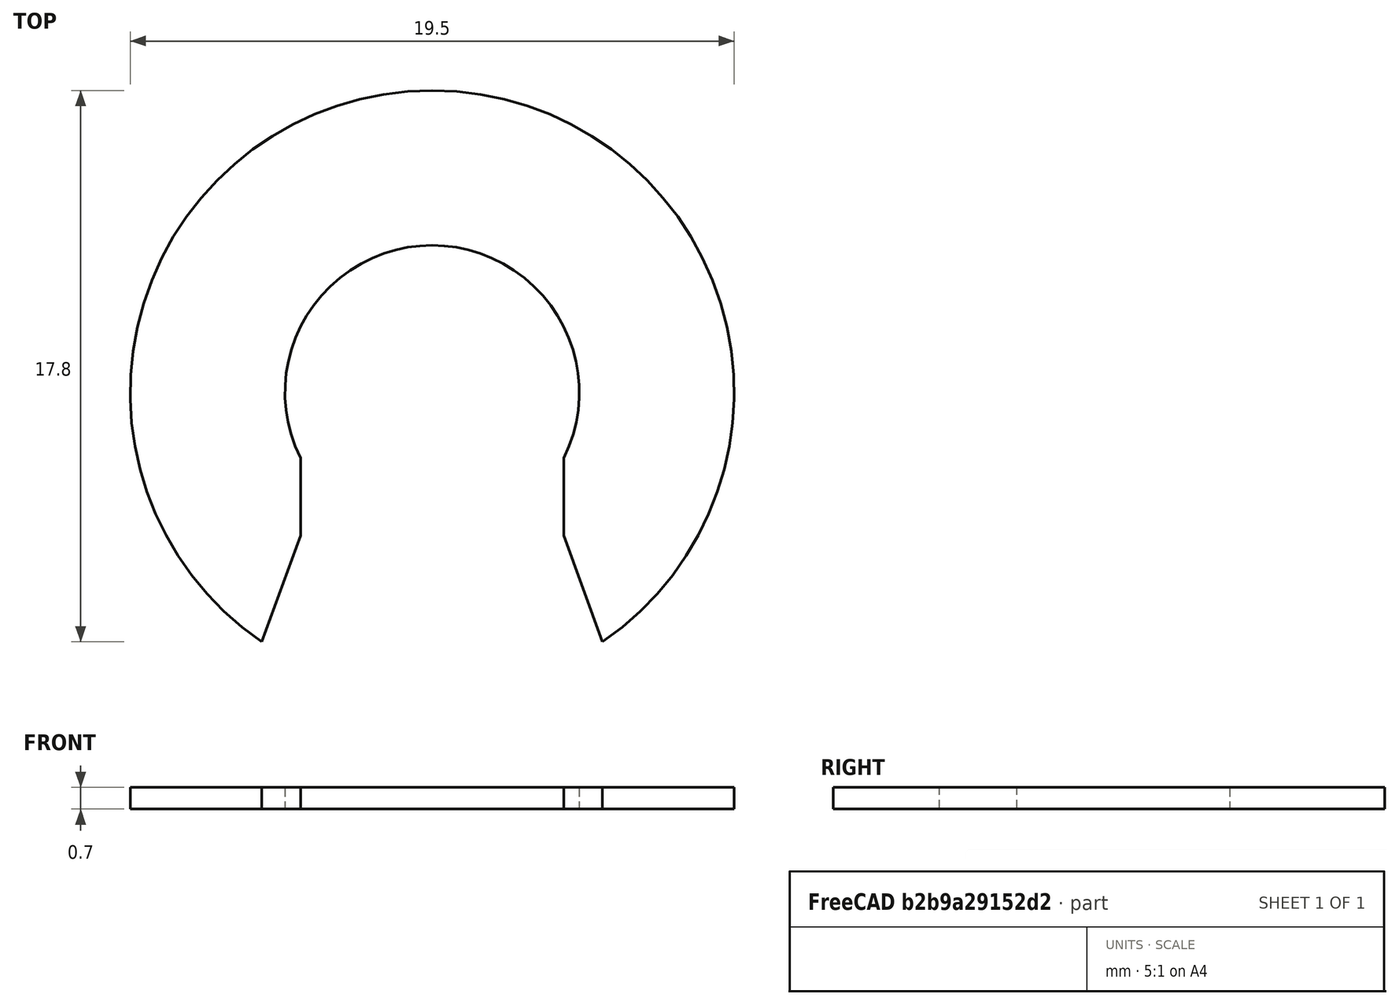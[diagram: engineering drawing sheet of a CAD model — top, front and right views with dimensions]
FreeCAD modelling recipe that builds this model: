
FCSTD DOCUMENT  (FreeCAD 0.21R30193 (Git))
Label: Clip
License: All rights reserved
LicenseURL: http://en.wikipedia.org/wiki/All_rights_reserved
objects: Sketcher::SketchObject×1, Part::Extrusion×1
note: 2 computed .brp shape members not serialized (recipe doc carries the construction recipe); baked Part::Feature solids carry a one-line shape summary decoded from their .brp

FEATURE [Sketcher::SketchObject] Sketch
  FullyConstrained = true
  sketch-geometry (6):
    g0: ArcOfCircle CenterX=0 CenterY=0 CenterZ=0 NormalX=0 NormalY=0 NormalZ=1 AngleXU=0 Radius=9.75 StartAngle=5.31173 EndAngle=10.3962
    g1: ArcOfCircle CenterX=0 CenterY=0 CenterZ=0 NormalX=0 NormalY=0 NormalZ=1 AngleXU=0 Radius=4.75 StartAngle=5.82023 EndAngle=9.88773
    g2: LineSegment StartX=-4.25 StartY=-2.12132 StartZ=0 EndX=-4.25 EndY=-4.62132 EndZ=0
    g3: LineSegment StartX=4.25 StartY=-2.12132 StartZ=0 EndX=4.25 EndY=-4.62132 EndZ=0
    g4: LineSegment StartX=4.25 StartY=-4.62132 StartZ=0 EndX=5.5 EndY=-8.05062 EndZ=0
    g5: LineSegment StartX=-5.5 StartY=-8.05062 StartZ=0 EndX=-4.25 EndY=-4.62132 EndZ=0
  constraints (17):
    c: Coincident(g0,g-1)
    c: Coincident(g1,g0)
    c: Coincident(g2,g1)
    c: Vertical(g2)
    c: Coincident(g3,g1)
    c: Vertical(g3)
    c: Coincident(g4,g3)
    c: Coincident(g4,g0)
    c: Coincident(g5,g0)
    c: Coincident(g5,g2)
    c: Symmetric(g2,g3,g-2)
    c: Diameter(g1) = 9.5
    c: Diameter(g0) = 19.5
    c: Symmetric(g0,g0,g-2)
    c: DistanceY(g3,g3) = 2.5
    c: DistanceX(g1,g1) = 8.5
    c: DistanceX(g0,g0) = 11
FEATURE [Part::Extrusion] Extrude
  Base = -> Sketch
  Dir = (0,0,1)
  DirMode = 2
  FaceMakerClass = Part::FaceMakerBullseye
  LengthFwd = 0.7
  LengthRev = 0
  Solid = true
  Symmetric = false
